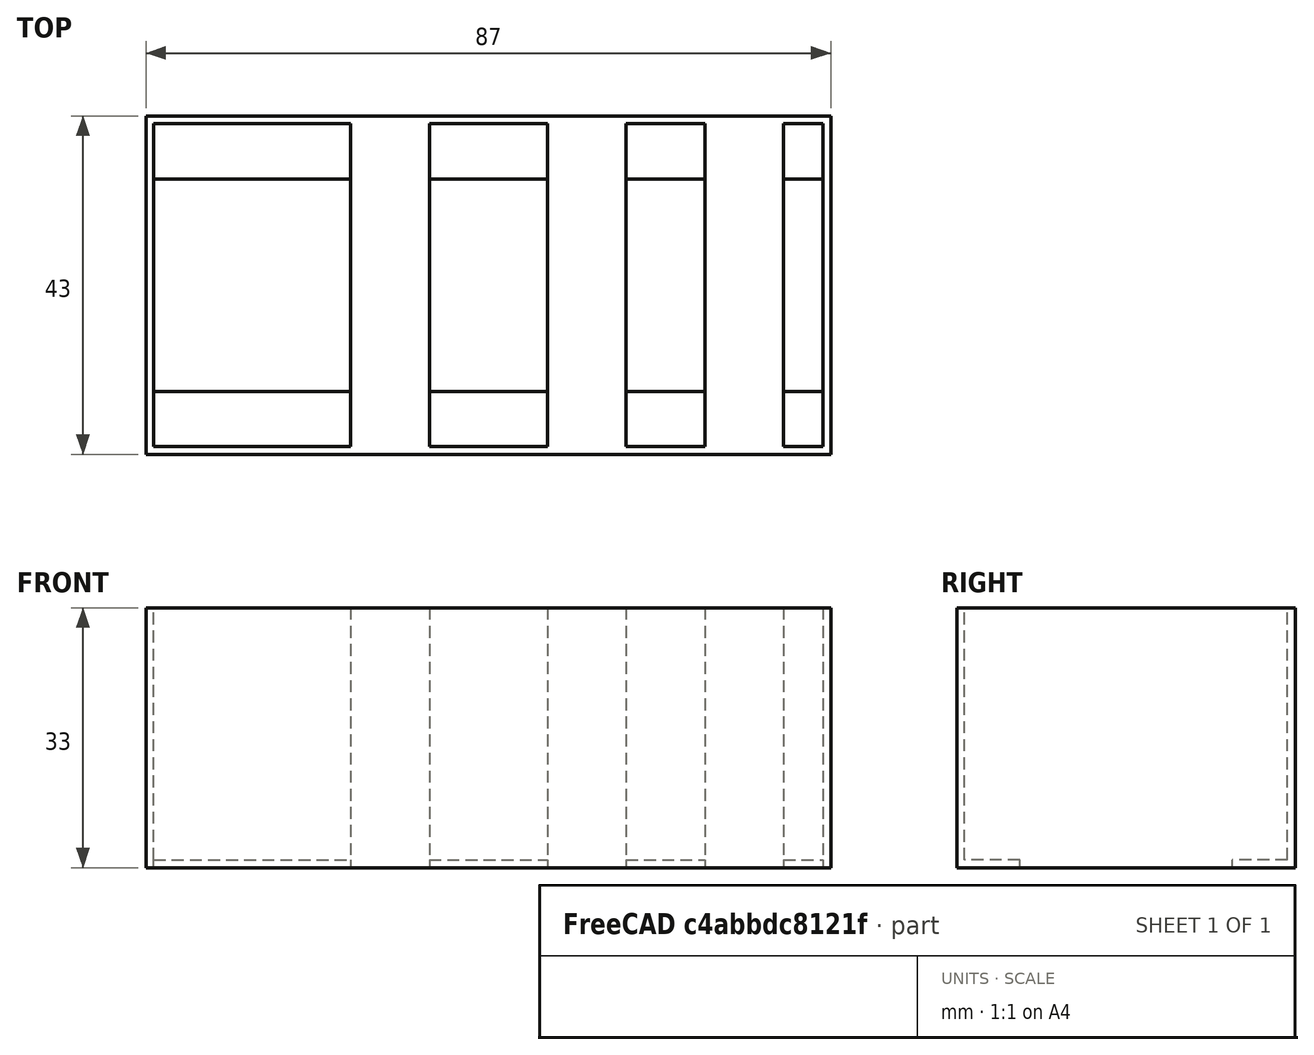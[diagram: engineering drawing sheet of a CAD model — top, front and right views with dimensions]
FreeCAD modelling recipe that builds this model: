
FCSTD DOCUMENT  (FreeCAD 0.18R4 (GitTag))
Label: cataclysm
License: All rights reserved
LicenseURL: http://en.wikipedia.org/wiki/All_rights_reserved
objects: Part::Box×9, Part::Cut×2, Part::MultiFuse×2
note: 13 computed .brp shape members not serialized (recipe doc carries the construction recipe); baked Part::Feature solids carry a one-line shape summary decoded from their .brp

FEATURE [Part::Box] Box  label="Cube"
  AttacherType = Attacher::AttachEngine3D
  Height = 33
  Length = 202
  Width = 43
FEATURE [Part::Box] Box001  label="Cube001"
  AttacherType = Attacher::AttachEngine3D
  Height = 33
  Length = 200
  Placement = pos=(1,1,0) rot=(0,0,1;0rad)
  Width = 41
FEATURE [Part::Cut] Cut
  Base = -> Box
  Tool = -> Box001
FEATURE [Part::Box] Box002  label="Cube002"
  AttacherType = Attacher::AttachEngine3D
  Height = 1
  Length = 202
  Width = 8
FEATURE [Part::Box] Box003  label="Cube003"
  AttacherType = Attacher::AttachEngine3D
  Height = 1
  Length = 202
  Placement = pos=(0,35,0) rot=(0,0,1;0rad)
  Width = 8
FEATURE [Part::MultiFuse] Fusion
  Shapes = -> [Cut,Box002,Box003]
FEATURE [Part::Box] Box004  label="Cube004"
  AttacherType = Attacher::AttachEngine3D
  Height = 33
  Length = 10
  Placement = pos=(26,0,0) rot=(0,0,1;0rad)
  Width = 43
FEATURE [Part::Box] Box005  label="Cube005"
  AttacherType = Attacher::AttachEngine3D
  Height = 33
  Length = 10
  Placement = pos=(51,0,0) rot=(0,0,1;0rad)
  Width = 43
FEATURE [Part::Box] Box006  label="Cube006"
  AttacherType = Attacher::AttachEngine3D
  Height = 33
  Length = 10
  Placement = pos=(71,0,0) rot=(0,0,1;0rad)
  Width = 43
FEATURE [Part::Box] Box007  label="Cube007"
  AttacherType = Attacher::AttachEngine3D
  Height = 33
  Length = 10
  Placement = pos=(86,0,0) rot=(0,0,1;0rad)
  Width = 43
FEATURE [Part::Box] Box008  label="Cube008"
  AttacherType = Attacher::AttachEngine3D
  Height = 33
  Length = 115
  Placement = pos=(87,0,0) rot=(0,0,1;0rad)
  Width = 43
FEATURE [Part::MultiFuse] Fusion001
  Shapes = -> [Fusion,Box004,Box005,Box006,Box007]
FEATURE [Part::Cut] Cut001
  Base = -> Fusion001
  Tool = -> Box008
